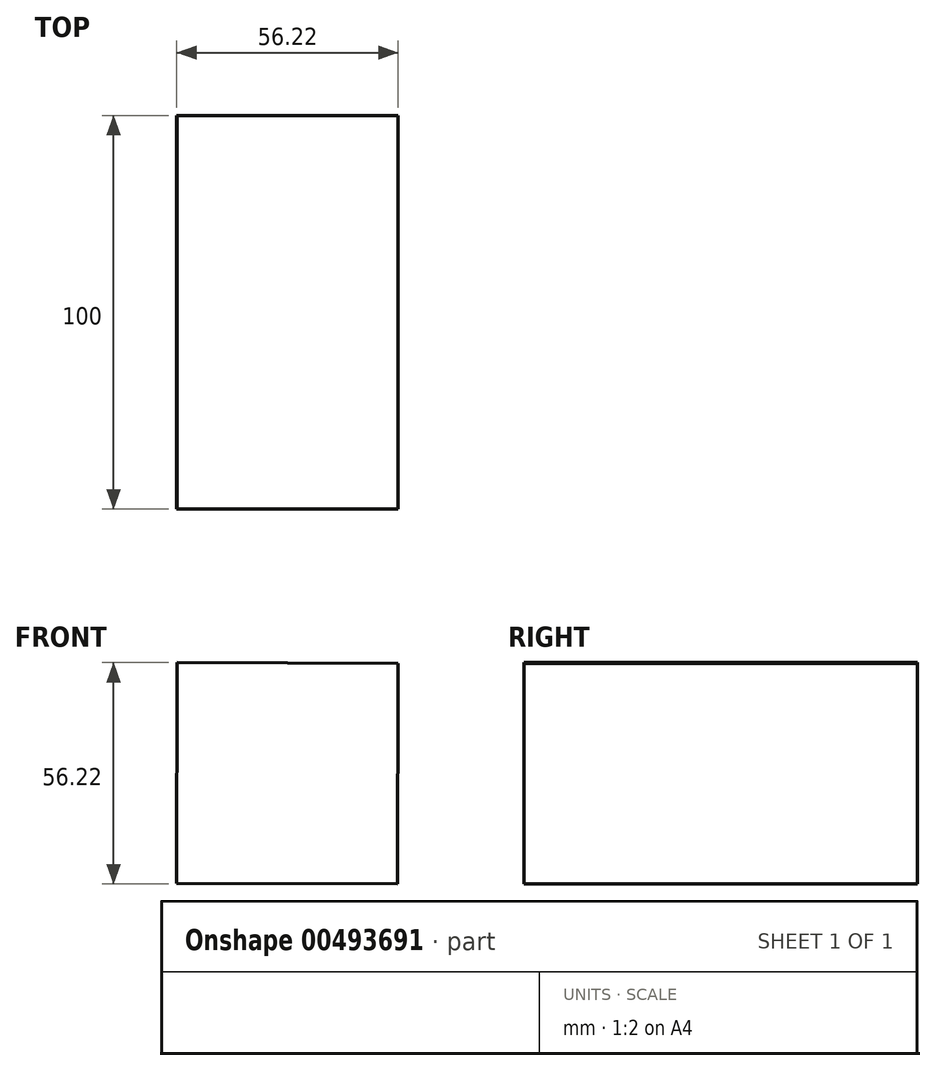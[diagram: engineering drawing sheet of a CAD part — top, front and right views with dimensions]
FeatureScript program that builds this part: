
annotation { "Feature Type Name" : "Feature", "Feature Type Description" : "" }
export const myFeature = defineFeature(function(context is Context, id is Id, definition is map)
    precondition{}
    {
        {
            var Q0;
            Q0=qCreatedBy(makeId("Front.planeOp"),FACE);
            var sketch = newSketch(context, id + "F0", { "sketchPlane" : qUnion([Q0])});
            skCircle(sketch, "E0.cCircle", {"center": v(0, 0) * mm, "radius": 39.66 * mm, "construction": true});
            skLineSegment(sketch, "E0.0", {"start": v(-27.97, 28.11) * mm, "end": v(28.11, 27.97) * mm});
            skLineSegment(sketch, "E0.1", {"start": v(28.11, 27.97) * mm, "end": v(27.97, -28.11) * mm});
            skLineSegment(sketch, "E0.2", {"start": v(27.97, -28.11) * mm, "end": v(-28.11, -27.97) * mm});
            skLineSegment(sketch, "E0.3", {"start": v(-28.11, -27.97) * mm, "end": v(-27.97, 28.11) * mm});
            skSolve(sketch);
        }
        {
            var Q0;
            Q0=makeQuery(id+"F0.imprint","IMPRINT",FACE,{"disambiguationData":[TD([[makeQuery(id+"F0.imprint","IMPRINT",EDGE,{"derivedFrom":sQuery(id+"F0.wireOp",EDGE,"E0.0")}),-1.0]])]});
            extrude(context, id + "F1", {"entities" : qUnion([Q0]), "depth" : 100 * mm});
        }
    });
